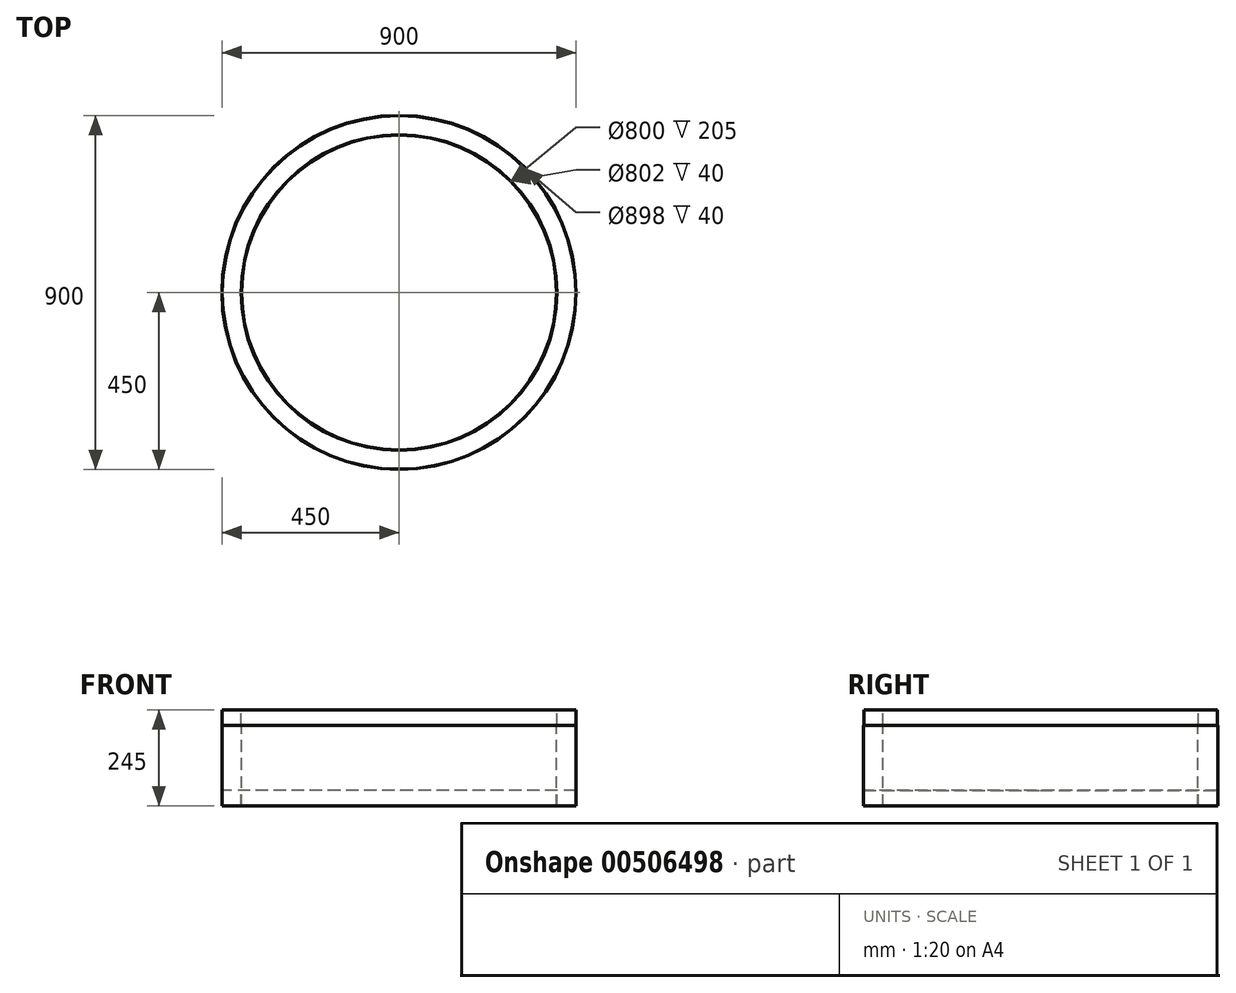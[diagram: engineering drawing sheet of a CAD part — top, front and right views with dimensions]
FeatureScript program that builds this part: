
annotation { "Feature Type Name" : "Feature", "Feature Type Description" : "" }
export const myFeature = defineFeature(function(context is Context, id is Id, definition is map)
    precondition{}
    {
        {
            var Q0;
            Q0=qCreatedBy(makeId("Front.planeOp"),FACE);
            var sketch = newSketch(context, id + "F0", { "sketchPlane" : qUnion([Q0])});
            skLineSegment(sketch, "E0", {"start": v(0, 74.87) * mm, "end": v(0, -73.71) * mm, "construction": true});
            skLineSegment(sketch, "E1", {"start": v(0, 374.84) * mm, "end": v(0, -528.94) * mm, "construction": true});
            skLineSegment(sketch, "E2", {"start": v(-400, -489.75) * mm, "end": v(-400, -284.75) * mm});
            skLineSegment(sketch, "E3", {"start": v(-400, -284.75) * mm, "end": v(-401, -284.75) * mm});
            skLineSegment(sketch, "E4", {"start": v(-401, -284.75) * mm, "end": v(-401, -244.75) * mm});
            skLineSegment(sketch, "E5", {"start": v(-401, -244.75) * mm, "end": v(-449, -244.75) * mm});
            skLineSegment(sketch, "E6", {"start": v(-449, -244.75) * mm, "end": v(-449, -284.75) * mm});
            skLineSegment(sketch, "E7", {"start": v(-449, -284.75) * mm, "end": v(-450, -284.75) * mm});
            skLineSegment(sketch, "E8", {"start": v(-450, -284.75) * mm, "end": v(-450, -489.75) * mm});
            skLineSegment(sketch, "E9", {"start": v(-450, -489.75) * mm, "end": v(-449, -489.75) * mm});
            skLineSegment(sketch, "E10", {"start": v(-449, -489.75) * mm, "end": v(-449, -449.75) * mm});
            skLineSegment(sketch, "E11", {"start": v(-449, -449.75) * mm, "end": v(-401, -449.75) * mm});
            skLineSegment(sketch, "E12", {"start": v(-401, -449.75) * mm, "end": v(-401, -489.75) * mm});
            skLineSegment(sketch, "E13", {"start": v(-401, -489.75) * mm, "end": v(-400, -489.75) * mm});
            skSolve(sketch);
        }
        {
            var Q0;
            Q0=qSketchRegion(id+"F0",true);
            var Q1;
            Q1=sQuery(id+"F0.wireOp",EDGE,"E1");
            revolve(context, id + "F1", {"entities" : qUnion([Q0]), "axis" : qUnion([Q1]), "revolveType" : RevolveType.FULL});
        }
    });
